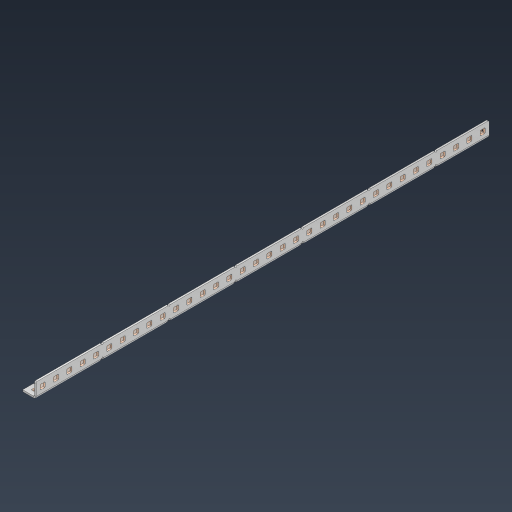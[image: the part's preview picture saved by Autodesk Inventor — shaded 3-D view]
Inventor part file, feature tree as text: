
AUTODESK INVENTOR PART (.ipt)
format: ipt  version: 2024.3 (Build 283343000, 343)  size: 1,239,552 bytes
history: native  units: in
note: dims shown in document units (in); Inventor stores cm internally (conversion verified against a paired STEP export)
features: other x109, extrude x100, sheet_metal_op x11, pattern_linear x2, mirror x1, chamfer x1, sketch x1
ambient origin geometry x8: Origin, YZ Plane, XZ Plane, XY Plane, X Axis, Y Axis, Z Axis, Center Point
bodies: Solid1 (feature_tree), Body (feature_tree)
feature tree (225):
  sheet_metal_op  "Flanges"
  other  "Flange Pattern Plane"
  other  "Flange Pattern Sketch"
  sheet_metal_op  "Flange Pattern"
  sheet_metal_op  "Body Pattern"
  pattern_linear  "Center Pattern"  Spacing1=17.0in  [1 undecoded]
  other  "Arc Length"
  mirror  "Notch Mirror"
  pattern_linear  "Notch Pattern"  Spacing1=0.0625in  [1 undecoded]
  chamfer  "End Chamfer"
  extrude  "Half Cut"  Depth=0.0625in
  other  "Plate1"
  sketch  "Sketch2"  dims[d0=1.0in d1=17.0in d2=0.0625in d3=0.0625in d4=0.0312in d5=0.125in d6=0.0625in d7=0.5in d8=90.0deg d9=0.0312in d10=0.25in d11=0.0625in d12=0.0625in d16=0.182in d17=0.02in d18=0.0625in d19=0.0in d20=0.25in d21=0.25in d38=13.3858in d40=0.5in d41=0.3937in d43=1.0in d46=0.172in d47=1.0in d48=0.0in d49=0.182in d50=0.02in d51=0.25in d52=0.25in d53=0.0625in d54=0.0in d55=0.172in d56=1.0in d57=0.0in d58=0.25in d60=13.3858in d62=0.5in d63=0.3937in d65=0.5in d85=0.1473in d86=0.1782in d88=0.04in d89=0.0625in d90=0.0in d91=0.04in d92=0.0491in d95=2.5in d96=0.04in d97=0.25in d98=45.0deg d99=0.25in d100=0.5in d101=0.0in d102=2.497in d106=0.182in d107=0.02in d108=0.5in d109=0.5in d110=0.0625in d111=0.0in d112=0.172in d113=0.5in d114=0.0in d117=0.5in d118=0.5in d119=0.5in]
  other  "Plate2"
  sheet_metal_op  "Bend1"
  sheet_metal_op  "Corner1"
  other  "Srf1"
  other  "Srf2"
  other  "Srf91"
  sheet_metal_op  "Body Pattern Sketch"
  other  "Srf92"
  other  "Srf786"
  other  "Srf823"
  other  "Srf824"
  other  "Srf825"
  other  "Srf826"
  other  "Srf827"
  other  "Srf828"
  other  "Srf829"
  other  "Srf856"
  other  "Srf857"
  other  "Srf858"
  other  "Srf859"
  other  "Srf860"
  other  "Srf861"
  other  "Srf862"
  other  "Srf889"
  other  "Srf890"
  other  "Srf891"
  other  "Srf892"
  other  "Srf893"
  other  "Srf894"
  other  "Srf895"
  other  "Srf896"
  other  "Srf922"
  other  "Srf923"
  other  "Srf924"
  other  "Srf925"
  other  "Srf926"
  other  "Srf959"
  other  "Srf960"
  other  "Srf961"
  other  "Srf962"
  other  "Srf963"
  other  "Srf996"
  other  "Srf997"
  other  "Srf998"
  other  "Srf999"
  other  "Srf1000"
  other  "Srf1143"
  other  "Srf1144"
  other  "Srf1145"
  other  "Srf1146"
  other  "Srf1147"
  other  "Srf1148"
  other  "Srf1149"
  other  "Srf1150"
  other  "Srf1151"
  other  "Srf1152"
  other  "Srf1153"
  other  "Srf1154"
  other  "Srf1155"
  other  "Srf1156"
  other  "Srf1157"
  other  "Srf1158"
  other  "Srf1159"
  other  "Srf1160"
  other  "Srf1161"
  other  "Srf1162"
  other  "Srf1199"
  other  "Srf1200"
  other  "Srf1201"
  other  "Srf1202"
  other  "Srf1203"
  other  "Srf1204"
  other  "Srf1205"
  other  "Srf1206"
  other  "Srf1207"
  other  "Srf1208"
  other  "Srf1209"
  other  "Srf1210"
  other  "Srf1211"
  other  "Srf1212"
  other  "Srf1213"
  other  "Srf1214"
  other  "Srf1215"
  other  "Srf1216"
  other  "Srf1217"
  other  "Srf1218"
  other  "Srf1255"
  other  "Srf1256"
  other  "Srf1257"
  other  "Srf1258"
  other  "Srf1259"
  other  "Srf1260"
  other  "Srf1261"
  other  "Srf1262"
  other  "Srf1263"
  other  "Srf1264"
  other  "Srf1265"
  other  "Srf1266"
  other  "Srf1267"
  other  "Srf1268"
  other  "Srf1269"
  other  "Srf1270"
  other  "Srf1271"
  other  "Srf1272"
  other  "Srf1273"
  other  "Srf1274"
  sheet_metal_op  "Flange Stamp"
  sheet_metal_op  "Flange Circle"
  sheet_metal_op  "Body Stamp"
  sheet_metal_op  "Body Circle"
  other  "Center Stamp"
  other  "Center Circle"
  sheet_metal_op  "Notch"
  extrude  "ExtrusionSrf2"  Depth=0.0312in
  extrude  "ExtrusionSrf92"  Depth=0.5in
  extrude  "ExtrusionSrf823"  Depth=0.0625in
  extrude  "ExtrusionSrf824"  Depth=0.5in TaperAngle=90.0deg
  extrude  "ExtrusionSrf825"  Depth=0.25in
  extrude  "ExtrusionSrf826"  Depth=0.0625in
  extrude  "ExtrusionSrf827"  Depth=0.0625in
  extrude  "ExtrusionSrf828"  Depth=0.182in
  extrude  "ExtrusionSrf829"  Depth=0.02in
  extrude  "ExtrusionSrf856"  Depth=0.0625in
  extrude  "ExtrusionSrf857"  TaperAngle=0.0deg  [1 undecoded]
  extrude  "ExtrusionSrf858"  Depth=0.25in
  extrude  "ExtrusionSrf859"  Depth=0.25in
  extrude  "ExtrusionSrf860"  Depth=0.5in
  extrude  "ExtrusionSrf861"  Depth=0.5in
  extrude  "ExtrusionSrf862"  Depth=1.0in TaperAngle=0.0deg
  extrude  "ExtrusionSrf889"  Depth=0.182in
  extrude  "ExtrusionSrf890"  Depth=0.02in
  extrude  "ExtrusionSrf891"  Depth=0.25in
  extrude  "ExtrusionSrf892"  Depth=0.25in
  extrude  "ExtrusionSrf893"  Depth=0.0625in
  extrude  "ExtrusionSrf894"  TaperAngle=0.0deg  [1 undecoded]
  extrude  "ExtrusionSrf895"  Depth=0.5in
  extrude  "ExtrusionSrf896"  Depth=1.0in TaperAngle=0.0deg
  extrude  "ExtrusionSrf922"  Depth=0.25in
  extrude  "ExtrusionSrf923"  Depth=0.5in
  extrude  "ExtrusionSrf924"  Depth=0.5in
  extrude  "ExtrusionSrf925"  Depth=0.5in
  extrude  "ExtrusionSrf926"  Depth=0.5in
  extrude  "ExtrusionSrf959"  Depth=0.5in
  extrude  "ExtrusionSrf960"  Depth=0.0625in
  extrude  "ExtrusionSrf961"  TaperAngle=0.0deg  [1 undecoded]
  extrude  "ExtrusionSrf962"  Depth=0.5in
  extrude  "ExtrusionSrf963"  Depth=0.5in
  extrude  "ExtrusionSrf996"  Depth=2.5in
  extrude  "ExtrusionSrf997"  Depth=0.25in TaperAngle=45.0deg
  extrude  "ExtrusionSrf998"  Depth=0.25in
  extrude  "ExtrusionSrf999"  Depth=0.5in TaperAngle=0.0deg
  extrude  "ExtrusionSrf1000"  Depth=0.5in
  extrude  "ExtrusionSrf1143"  Depth=0.182in
  extrude  "ExtrusionSrf1144"  Depth=0.02in
  extrude  "ExtrusionSrf1145"  Depth=0.5in
  extrude  "ExtrusionSrf1146"  Depth=0.5in
  extrude  "ExtrusionSrf1147"  Depth=0.0625in
  extrude  "ExtrusionSrf1148"  TaperAngle=0.0deg  [1 undecoded]
  extrude  "ExtrusionSrf1149"  Depth=0.5in
  extrude  "ExtrusionSrf1150"  Depth=0.5in TaperAngle=0.0deg
  extrude  "ExtrusionSrf1151"  Depth=0.5in
  extrude  "ExtrusionSrf1152"  Depth=0.5in
  extrude  "ExtrusionSrf1153"  Depth=0.5in
  extrude  "ExtrusionSrf1154"  [1 undecoded]
  extrude  "ExtrusionSrf1155"  [1 undecoded]
  extrude  "ExtrusionSrf1156"  [1 undecoded]
  extrude  "ExtrusionSrf1157"  [1 undecoded]
  extrude  "ExtrusionSrf1158"  [1 undecoded]
  extrude  "ExtrusionSrf1159"  [1 undecoded]
  extrude  "ExtrusionSrf1160"  [1 undecoded]
  extrude  "ExtrusionSrf1161"  [1 undecoded]
  extrude  "ExtrusionSrf1162"  [1 undecoded]
  extrude  "ExtrusionSrf1199"  [1 undecoded]
  extrude  "ExtrusionSrf1200"  [1 undecoded]
  extrude  "ExtrusionSrf1201"  [1 undecoded]
  extrude  "ExtrusionSrf1202"  [1 undecoded]
  extrude  "ExtrusionSrf1203"  [1 undecoded]
  extrude  "ExtrusionSrf1204"  [1 undecoded]
  extrude  "ExtrusionSrf1205"  [1 undecoded]
  extrude  "ExtrusionSrf1206"  [1 undecoded]
  extrude  "ExtrusionSrf1207"  [1 undecoded]
  extrude  "ExtrusionSrf1208"  [1 undecoded]
  extrude  "ExtrusionSrf1209"  [1 undecoded]
  extrude  "ExtrusionSrf1210"  [1 undecoded]
  extrude  "ExtrusionSrf1211"  [1 undecoded]
  extrude  "ExtrusionSrf1212"  [1 undecoded]
  extrude  "ExtrusionSrf1213"  [1 undecoded]
  extrude  "ExtrusionSrf1214"  [1 undecoded]
  extrude  "ExtrusionSrf1215"  [1 undecoded]
  extrude  "ExtrusionSrf1216"  [1 undecoded]
  extrude  "ExtrusionSrf1217"  [1 undecoded]
  extrude  "ExtrusionSrf1218"  [1 undecoded]
  extrude  "ExtrusionSrf1255"  [1 undecoded]
  extrude  "ExtrusionSrf1256"  [1 undecoded]
  extrude  "ExtrusionSrf1257"  [1 undecoded]
  extrude  "ExtrusionSrf1258"  [1 undecoded]
  extrude  "ExtrusionSrf1259"  [1 undecoded]
  extrude  "ExtrusionSrf1260"  [1 undecoded]
  extrude  "ExtrusionSrf1261"  [1 undecoded]
  extrude  "ExtrusionSrf1262"  [1 undecoded]
  extrude  "ExtrusionSrf1263"  [1 undecoded]
  extrude  "ExtrusionSrf1264"  [1 undecoded]
  extrude  "ExtrusionSrf1265"  [1 undecoded]
  extrude  "ExtrusionSrf1266"  [1 undecoded]
  extrude  "ExtrusionSrf1267"  [1 undecoded]
  extrude  "ExtrusionSrf1268"  [1 undecoded]
  extrude  "ExtrusionSrf1269"  [1 undecoded]
  extrude  "ExtrusionSrf1270"  [1 undecoded]
  extrude  "ExtrusionSrf1271"  [1 undecoded]
  extrude  "ExtrusionSrf1272"  [1 undecoded]
  extrude  "ExtrusionSrf1273"  [1 undecoded]
  extrude  "ExtrusionSrf1274"  [1 undecoded]
note: 55 required parameter values undecoded (feature->parameter linkage not recoverable at this tier; creation-order binding heuristic only, values carry confidence <= 0.55)
